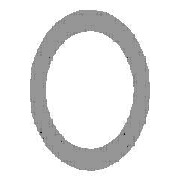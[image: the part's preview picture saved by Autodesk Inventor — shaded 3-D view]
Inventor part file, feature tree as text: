
AUTODESK INVENTOR PART (.ipt)
format: ipt  version: 2013 (Build 170138000, 138)  size: 134,656 bytes
history: native  units: mm (DEFAULTED — no unit token found)
features: plane x6, sketch x6, other x4, extrude x3
ambient origin geometry x8: Origin, YZ Plane, XZ Plane, XY Plane, X Axis, Y Axis, Z Axis, Center Point
bodies: Solid1 (feature_tree), Body (feature_tree)
feature tree (19):
  parser-record x1  (decoder bookkeeping rows leaked as tree rows — omitted from the tree; the rows remain in map.json)
  other  "Driven Length"
  other  "Start plane"
  other  "End plane"
  plane  "Work Plane4"
  plane  "Work Plane5"
  plane  "Work Plane6"
  extrude  "Extrusion2"  Depth=3.3782mm
  plane  "Work Plane7"
  extrude  "Extrusion3"  TaperAngle=0.0deg  [1 undecoded]
  plane  "Work Plane8"
  extrude  "Extrusion4"  TaperAngle=90.0deg  [1 undecoded]
  sketch  "Sketch"  dims[d10=25.4mm d11=0.0mm d12=6.35mm d13=39.6875mm d14=0.0mm]
  sketch  "Sketch3"  dims[d0=33.401mm d1=3.3782mm]
  plane  "Work Plane3"
  sketch  "Sketch4"  dims[d2=800.1mm d3=0.0mm d4=-0.0mm]
  sketch  "Sketch5"  dims[d5=800.1mm d6=90.0deg]
  sketch  "Sketch6"  dims[d7=800.1mm]
  sketch  "Sketch7"  dims[d8=3.302mm d9=0.0mm]
note: 2 required parameter values undecoded (feature->parameter linkage not recoverable at this tier; creation-order binding heuristic only, values carry confidence <= 0.55)
